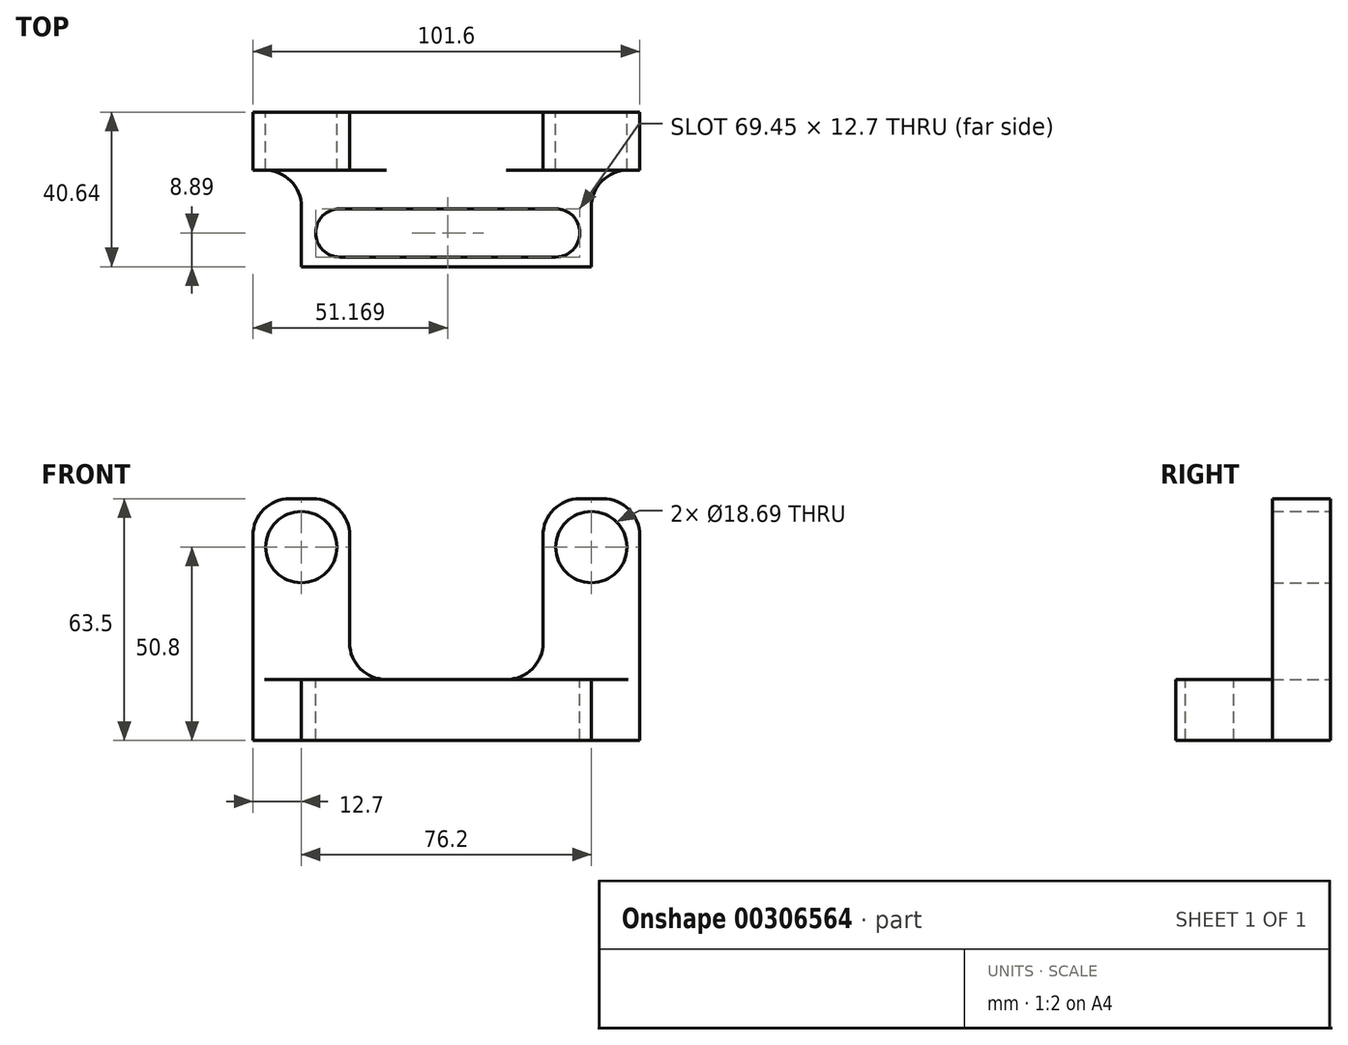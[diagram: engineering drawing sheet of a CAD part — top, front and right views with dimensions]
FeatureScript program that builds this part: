
annotation { "Feature Type Name" : "Feature", "Feature Type Description" : "" }
export const myFeature = defineFeature(function(context is Context, id is Id, definition is map)
    precondition{}
    {
        {
            var Q0;
            Q0=qCreatedBy(makeId("Front.planeOp"),FACE);
            var sketch = newSketch(context, id + "F0", { "sketchPlane" : qUnion([Q0])});
            skLineSegment(sketch, "E0", {"start": v(0, 0) * mm, "end": v(0, 63.5) * mm});
            skLineSegment(sketch, "E1", {"start": v(0, 63.5) * mm, "end": v(25.4, 63.5) * mm});
            skLineSegment(sketch, "E2", {"start": v(0, 0) * mm, "end": v(101.6, 0) * mm});
            skLineSegment(sketch, "E3", {"start": v(101.6, 0) * mm, "end": v(101.6, 63.5) * mm});
            skLineSegment(sketch, "E4", {"start": v(101.6, 63.5) * mm, "end": v(76.2, 63.5) * mm});
            skLineSegment(sketch, "E5", {"start": v(25.4, 63.5) * mm, "end": v(25.4, 16) * mm});
            skLineSegment(sketch, "E6", {"start": v(76.2, 63.5) * mm, "end": v(76.2, 16) * mm});
            skLineSegment(sketch, "E7", {"start": v(76.2, 16) * mm, "end": v(25.4, 16) * mm});
            skSolve(sketch);
        }
        {
            var Q0;
            Q0=makeQuery(id+"F0.imprint","IMPRINT",FACE,{"disambiguationData":[TD([[makeQuery(id+"F0.imprint","IMPRINT",EDGE,{"derivedFrom":sQuery(id+"F0.wireOp",EDGE,"E0")}),-1.0]])]});
            var sketch = newSketch(context, id + "F1", { "sketchPlane" : qUnion([Q0])});
            skCircle(sketch, "E8", {"center": v(12.7, 50.8) * mm, "radius": 9.34 * mm});
            skCircle(sketch, "E9", {"center": v(88.9, 50.8) * mm, "radius": 9.34 * mm});
            skSolve(sketch);
        }
        {
            var Q0;
            Q0=makeQuery(id+"F0.imprint","IMPRINT",FACE,{"disambiguationData":[TD([[makeQuery(id+"F0.imprint","IMPRINT",EDGE,{"derivedFrom":sQuery(id+"F0.wireOp",EDGE,"E0")}),-1.0]])]});
            extrude(context, id + "F2", {"entities" : qUnion([Q0]), "depth" : 40.64 * mm});
        }
        {
            var Q0;
            Q0=makeQuery(id+"F1.imprint","IMPRINT",FACE,{"disambiguationData":[TD([[makeQuery(id+"F1.imprint","IMPRINT",EDGE,{"derivedFrom":sQuery(id+"F1.wireOp",EDGE,"E8")}),1.0]])]});
            var Q1;
            Q1=makeQuery(id+"F1.imprint","IMPRINT",FACE,{"disambiguationData":[TD([[makeQuery(id+"F1.imprint","IMPRINT",EDGE,{"derivedFrom":sQuery(id+"F1.wireOp",EDGE,"E9")}),1.0]])]});
            extrude(context, id + "F3", {"entities" : qUnion([Q0, Q1]), "operationType" : NewBodyOperationType.REMOVE, "endBound" : BoundingType.THROUGH_ALL, "depth" : 25.4 * mm});
        }
        {
            var Q0;
            Q0=qCreatedBy(makeId("Top.planeOp"),FACE);
            var sketch = newSketch(context, id + "F4", { "sketchPlane" : qUnion([Q0])});
            skLineSegment(sketch, "E10.bottom", {"start": v(0, -15.24) * mm, "end": v(101.6, -15.24) * mm});
            skLineSegment(sketch, "E10.top", {"start": v(0, -40.64) * mm, "end": v(101.6, -40.64) * mm});
            skLineSegment(sketch, "E10.left", {"start": v(0, -15.24) * mm, "end": v(0, -40.64) * mm});
            skLineSegment(sketch, "E10.right", {"start": v(101.6, -15.24) * mm, "end": v(101.6, -40.64) * mm});
            skSolve(sketch);
        }
        {
            var Q0;
            Q0=makeQuery(id+"F4.imprint","IMPRINT",FACE,{"disambiguationData":[TD([[makeQuery(id+"F4.imprint","IMPRINT",EDGE,{"derivedFrom":sQuery(id+"F4.wireOp",EDGE,"E10.bottom")}),-1.0]])]});
            extrude(context, id + "F5", {"entities" : qUnion([Q0]), "operationType" : NewBodyOperationType.REMOVE, "endBound" : BoundingType.THROUGH_ALL, "depth" : 25.4 * mm, "hasSecondDirection" : true, "secondDirectionOppositeDirection" : false, "secondDirectionDepth" : 16 * mm});
        }
        {
            var Q0;
            Q0=makeQuery(id+"F2.opExtrude","CAP_FACE",FACE,{"disambiguationData":[OSD([sQuery(id+"F0.wireOp",EDGE,"E0"),sQuery(id+"F0.wireOp",EDGE,"E1"),sQuery(id+"F0.wireOp",EDGE,"E2"),sQuery(id+"F0.wireOp",EDGE,"E3"),sQuery(id+"F0.wireOp",EDGE,"E4"),sQuery(id+"F0.wireOp",EDGE,"E5"),sQuery(id+"F0.wireOp",EDGE,"E6"),sQuery(id+"F0.wireOp",EDGE,"E7")])],"isStart":false});
            var sketch = newSketch(context, id + "F6", { "sketchPlane" : qUnion([Q0])});
            skLineSegment(sketch, "E11.bottom", {"start": v(0, 16) * mm, "end": v(12.7, 16) * mm});
            skLineSegment(sketch, "E11.top", {"start": v(0, 0) * mm, "end": v(12.7, 0) * mm});
            skLineSegment(sketch, "E11.left", {"start": v(0, 16) * mm, "end": v(0, 0) * mm});
            skLineSegment(sketch, "E11.right", {"start": v(12.7, 16) * mm, "end": v(12.7, 0) * mm});
            skLineSegment(sketch, "E12.bottom", {"start": v(101.6, 16) * mm, "end": v(88.9, 16) * mm});
            skLineSegment(sketch, "E12.top", {"start": v(101.6, 0) * mm, "end": v(88.9, 0) * mm});
            skLineSegment(sketch, "E12.left", {"start": v(101.6, 16) * mm, "end": v(101.6, 0) * mm});
            skLineSegment(sketch, "E12.right", {"start": v(88.9, 16) * mm, "end": v(88.9, 0) * mm});
            skSolve(sketch);
        }
        {
            var Q0;
            Q0=makeQuery(id+"F6.imprint","IMPRINT",FACE,{"disambiguationData":[TD([[makeQuery(id+"F6.imprint","IMPRINT",EDGE,{"derivedFrom":sQuery(id+"F6.wireOp",EDGE,"E11.bottom")}),1.0]])]});
            var Q1;
            Q1=makeQuery(id+"F6.imprint","IMPRINT",FACE,{"disambiguationData":[TD([[makeQuery(id+"F6.imprint","IMPRINT",EDGE,{"derivedFrom":sQuery(id+"F6.wireOp",EDGE,"E12.bottom")}),1.0]])]});
            extrude(context, id + "F7", {"entities" : qUnion([Q0, Q1]), "operationType" : NewBodyOperationType.REMOVE, "oppositeDirection" : true, "depth" : 25.4 * mm});
        }
        {
            var Q0;
            Q0=makeQuery(id+"F2.opExtrude","SWEPT_EDGE",EDGE,{"disambiguationData":[OSD([sQuery(id+"F0.wireOp",EDGE,"E1"),sQuery(id+"F0.wireOp",EDGE,"E5")])]});
            var Q1;
            Q1=makeQuery(id+"F2.opExtrude","SWEPT_EDGE",EDGE,{"disambiguationData":[OSD([sQuery(id+"F0.wireOp",EDGE,"E0"),sQuery(id+"F0.wireOp",EDGE,"E1")])]});
            var Q2;
            Q2=makeQuery(id+"F2.opExtrude","SWEPT_EDGE",EDGE,{"disambiguationData":[OSD([sQuery(id+"F0.wireOp",EDGE,"E4"),sQuery(id+"F0.wireOp",EDGE,"E6")])]});
            var Q3;
            Q3=makeQuery(id+"F2.opExtrude","SWEPT_EDGE",EDGE,{"disambiguationData":[OSD([sQuery(id+"F0.wireOp",EDGE,"E3"),sQuery(id+"F0.wireOp",EDGE,"E4")])]});
            fillet(context, id + "F8", {"entities" : qUnion([Q0, Q1, Q2, Q3]), "radius" : 9.65 * mm, "tangentPropagation" : true, "allowEdgeOverflow" : false});
        }
        {
            var Q0;
            Q0=makeQuery(id+"F7.boolean.opBoolean","COPY",EDGE,{"derivedFrom":makeQuery(id+"F7.opExtrude","CAP_EDGE",EDGE,{"disambiguationData":[OSD([sQuery(id+"F6.wireOp",EDGE,"E11.right")])],"isStart":true})});
            var Q1;
            Q1=makeQuery(id+"F7.boolean.opBoolean","COPY",EDGE,{"derivedFrom":makeQuery(id+"F7.opExtrude","CAP_EDGE",EDGE,{"disambiguationData":[OSD([sQuery(id+"F6.wireOp",EDGE,"E12.right")])],"isStart":true})});
            var Q2;
            Q2=makeQuery(id+"F7.boolean.opBoolean","COPY",EDGE,{"derivedFrom":makeQuery(id+"F7.opExtrude","CAP_EDGE",EDGE,{"disambiguationData":[OSD([sQuery(id+"F6.wireOp",EDGE,"E11.right")])],"isStart":false})});
            var Q3;
            Q3=makeQuery(id+"F7.boolean.opBoolean","COPY",EDGE,{"derivedFrom":makeQuery(id+"F7.opExtrude","CAP_EDGE",EDGE,{"disambiguationData":[OSD([sQuery(id+"F6.wireOp",EDGE,"E12.right")])],"isStart":false})});
            fillet(context, id + "F9", {"entities" : qUnion([Q0, Q1, Q2, Q3]), "radius" : 9.65 * mm, "tangentPropagation" : true, "allowEdgeOverflow" : false});
        }
        {
            var Q0;
            Q0=makeQuery(id+"F5.boolean.opBoolean","MERGE",FACE,{"derivedFrom":[makeQuery(id+"F2.opExtrude","SWEPT_FACE",FACE,{"disambiguationData":[OSD([sQuery(id+"F0.wireOp",EDGE,"E7")])]}),makeQuery(id+"F5.opExtrude","CAP_FACE",FACE,{"disambiguationData":[OSD([sQuery(id+"F4.wireOp",EDGE,"E10.bottom"),sQuery(id+"F4.wireOp",EDGE,"E10.top"),sQuery(id+"F4.wireOp",EDGE,"E10.left"),sQuery(id+"F4.wireOp",EDGE,"E10.right")])],"isStart":true})]});
            var sketch = newSketch(context, id + "F10", { "sketchPlane" : qUnion([Q0])});
            skLineSegment(sketch, "E13.bottom", {"start": v(22.8, -38.1) * mm, "end": v(79.54, -38.1) * mm});
            skLineSegment(sketch, "E13.top", {"start": v(22.8, -25.4) * mm, "end": v(79.54, -25.4) * mm});
            skArc(sketch, "E14", {"start": v(22.8, -25.4) * mm, "mid": v(16.44, -31.75) * mm, "end": v(22.8, -38.1) * mm});
            skArc(sketch, "E15", {"start": v(79.54, -38.1) * mm, "mid": v(85.9, -31.75) * mm, "end": v(79.54, -25.4) * mm});
            skSolve(sketch);
        }
        {
            var Q0;
            Q0=makeQuery(id+"F10.imprint","IMPRINT",FACE,{"disambiguationData":[TD([[makeQuery(id+"F10.imprint","IMPRINT",EDGE,{"derivedFrom":sQuery(id+"F10.wireOp",EDGE,"E13.bottom")}),1.0]])]});
            extrude(context, id + "F11", {"entities" : qUnion([Q0]), "operationType" : NewBodyOperationType.REMOVE, "endBound" : BoundingType.THROUGH_ALL, "oppositeDirection" : true, "depth" : 25.4 * mm});
        }
        {
            var Q0;
            Q0=makeQuery(id+"F2.opExtrude","SWEPT_EDGE",EDGE,{"disambiguationData":[OSD([sQuery(id+"F0.wireOp",EDGE,"E5"),sQuery(id+"F0.wireOp",EDGE,"E7")])]});
            var Q1;
            Q1=makeQuery(id+"F2.opExtrude","SWEPT_EDGE",EDGE,{"disambiguationData":[OSD([sQuery(id+"F0.wireOp",EDGE,"E6"),sQuery(id+"F0.wireOp",EDGE,"E7")])]});
            fillet(context, id + "F12", {"entities" : qUnion([Q0, Q1]), "radius" : 9.65 * mm, "tangentPropagation" : true, "allowEdgeOverflow" : false});
        }
    });
